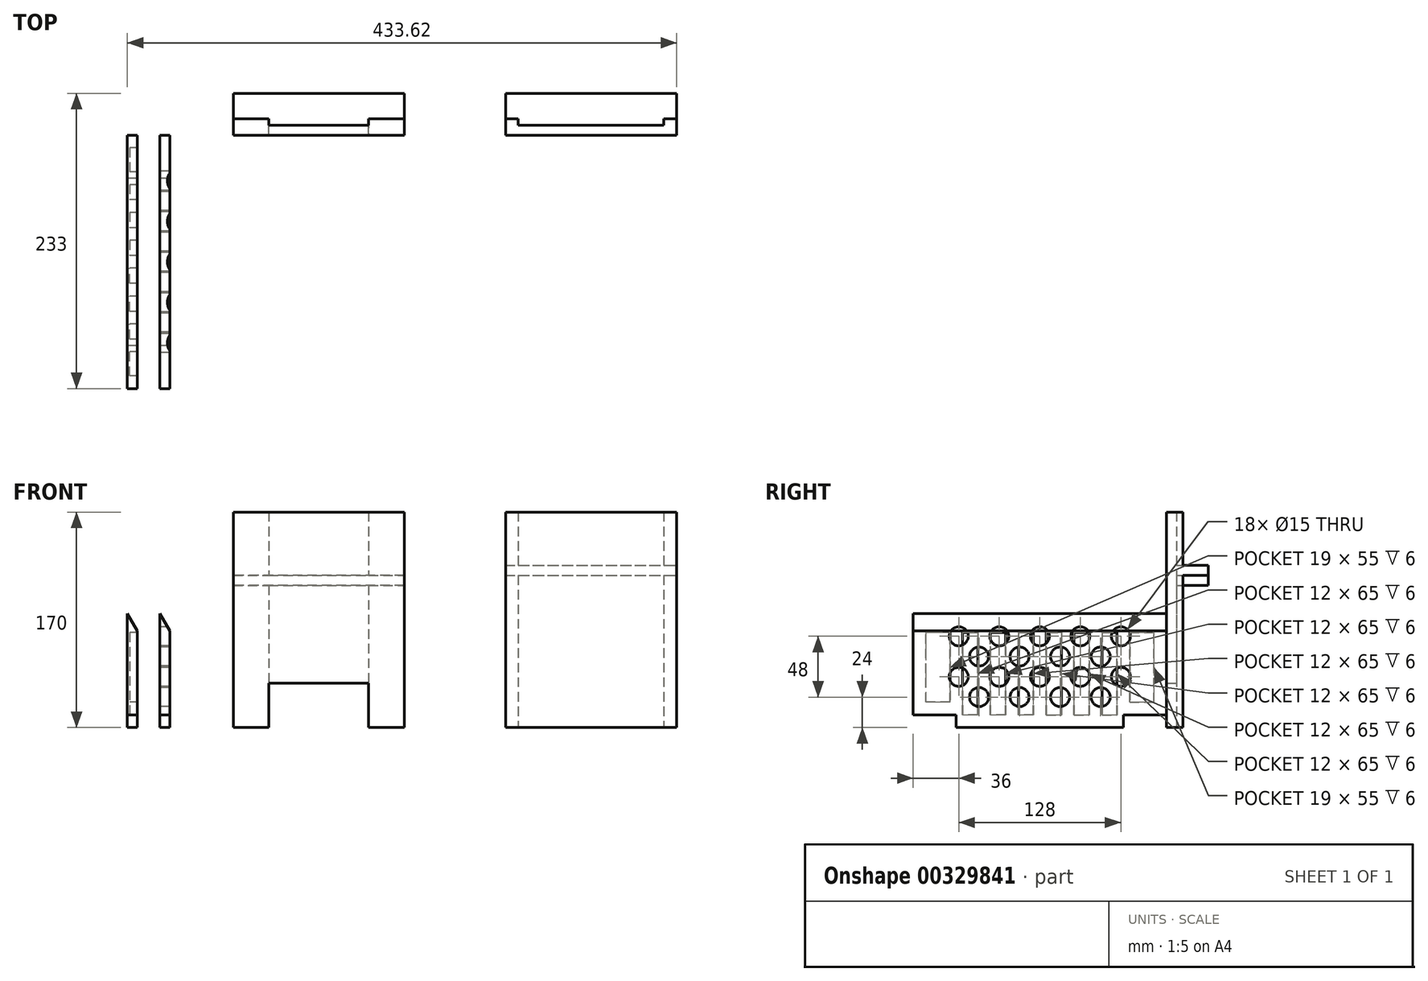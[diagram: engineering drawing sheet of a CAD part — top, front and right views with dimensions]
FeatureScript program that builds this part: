
annotation { "Feature Type Name" : "Feature", "Feature Type Description" : "" }
export const myFeature = defineFeature(function(context is Context, id is Id, definition is map)
    precondition{}
    {
        {
            var Q0;
            Q0=qCreatedBy(makeId("Top.planeOp"),FACE);
            var sketch = newSketch(context, id + "F0", { "sketchPlane" : qUnion([Q0])});
            skLineSegment(sketch, "E0", {"start": v(40, 13) * mm, "end": v(40, 0) * mm});
            skLineSegment(sketch, "E1", {"start": v(40, 0) * mm, "end": v(175, 0) * mm});
            skLineSegment(sketch, "E2", {"start": v(175, 0) * mm, "end": v(175, 13) * mm});
            skLineSegment(sketch, "E3", {"start": v(175, 13) * mm, "end": v(165, 13) * mm});
            skLineSegment(sketch, "E4", {"start": v(165, 13) * mm, "end": v(165, 8) * mm});
            skLineSegment(sketch, "E5", {"start": v(165, 8) * mm, "end": v(50, 8) * mm});
            skLineSegment(sketch, "E6", {"start": v(50, 8) * mm, "end": v(50, 13) * mm});
            skLineSegment(sketch, "E7", {"start": v(50, 13) * mm, "end": v(40, 13) * mm});
            skSolve(sketch);
        }
        {
            var Q0;
            Q0 = qSketchRegion(id + "F0", true);
            extrude(context, id + "F1", {"entities" : qUnion([Q0]), "depth" : 170 * mm, "offsetDistance" : 25 * mm});
        }
        {
            var Q0;
            Q0=makeQuery(id+"F1.opExtrude","CAP_FACE",FACE,{"disambiguationData":[OSD([sQuery(id+"F0.wireOp",EDGE,"E0"),sQuery(id+"F0.wireOp",EDGE,"E1"),sQuery(id+"F0.wireOp",EDGE,"E2"),sQuery(id+"F0.wireOp",EDGE,"E3"),sQuery(id+"F0.wireOp",EDGE,"E4"),sQuery(id+"F0.wireOp",EDGE,"E5"),sQuery(id+"F0.wireOp",EDGE,"E6"),sQuery(id+"F0.wireOp",EDGE,"E7")])],"isStart":true});
            cPlane(context, id + "F2", {"entities" : qUnion([Q0]), "cplaneType" : CPlaneType.OFFSET, "offset" : 120 * mm, "oppositeDirection" : true, "width" : 150 * mm, "height" : 150 * mm});
        }
        {
            var Q0;
            Q0=qCreatedBy(id+"F2.planeOp",FACE);
            var sketch = newSketch(context, id + "F3", { "sketchPlane" : qUnion([Q0])});
            skLineSegment(sketch, "E8.bottom", {"start": v(40, 0) * mm, "end": v(175, 0) * mm});
            skLineSegment(sketch, "E8.top", {"start": v(40, -33) * mm, "end": v(175, -33) * mm});
            skLineSegment(sketch, "E8.left", {"start": v(40, 0) * mm, "end": v(40, -33) * mm});
            skLineSegment(sketch, "E8.right", {"start": v(175, 0) * mm, "end": v(175, -33) * mm});
            skSolve(sketch);
        }
        {
            var Q0;
            Q0 = qSketchRegion(id + "F3", true);
            extrude(context, id + "F4", {"entities" : qUnion([Q0]), "operationType" : NewBodyOperationType.ADD, "oppositeDirection" : true, "depth" : 8 * mm, "offsetDistance" : 25 * mm});
        }
        {
            var Q0;
            Q0=qCreatedBy(makeId("Top.planeOp"),FACE);
            var sketch = newSketch(context, id + "F5", { "sketchPlane" : qUnion([Q0])});
            skLineSegment(sketch, "E9", {"start": v(-40, 0) * mm, "end": v(-40, 13) * mm});
            skLineSegment(sketch, "E10", {"start": v(-40, 13) * mm, "end": v(-68, 13) * mm});
            skLineSegment(sketch, "E11", {"start": v(-68, 13) * mm, "end": v(-68, 8) * mm});
            skLineSegment(sketch, "E12", {"start": v(-68, 8) * mm, "end": v(-147, 8) * mm});
            skLineSegment(sketch, "E13", {"start": v(-147, 8) * mm, "end": v(-147, 13) * mm});
            skLineSegment(sketch, "E14", {"start": v(-147, 13) * mm, "end": v(-175, 13) * mm});
            skLineSegment(sketch, "E15", {"start": v(-175, 13) * mm, "end": v(-175, 0) * mm});
            skLineSegment(sketch, "E16", {"start": v(-175, 0) * mm, "end": v(-40, 0) * mm});
            skSolve(sketch);
        }
        {
            var Q0;
            Q0 = qSketchRegion(id + "F5", true);
            extrude(context, id + "F6", {"entities" : qUnion([Q0]), "depth" : 170 * mm, "offsetDistance" : 25 * mm});
        }
        {
            var Q0;
            Q0=makeQuery(id+"F6.opExtrude","SWEPT_FACE",FACE,{"disambiguationData":[OSD([sQuery(id+"F5.wireOp",EDGE,"E12")])]});
            var sketch = newSketch(context, id + "F7", { "sketchPlane" : qUnion([Q0])});
            skLineSegment(sketch, "E17.bottom", {"start": v(68, 0) * mm, "end": v(147, 0) * mm});
            skLineSegment(sketch, "E17.top", {"start": v(68, 35) * mm, "end": v(147, 35) * mm});
            skLineSegment(sketch, "E17.left", {"start": v(68, 0) * mm, "end": v(68, 35) * mm});
            skLineSegment(sketch, "E17.right", {"start": v(147, 0) * mm, "end": v(147, 35) * mm});
            skSolve(sketch);
        }
        {
            var Q0;
            Q0 = qSketchRegion(id + "F7", true);
            extrude(context, id + "F8", {"entities" : qUnion([Q0]), "operationType" : NewBodyOperationType.REMOVE, "endBound" : BoundingType.UP_TO_NEXT, "oppositeDirection" : true, "depth" : 25 * mm, "offsetDistance" : 25 * mm});
        }
        {
            var Q0;
            Q0=qCreatedBy(id+"F2.planeOp",FACE);
            var sketch = newSketch(context, id + "F9", { "sketchPlane" : qUnion([Q0])});
            skLineSegment(sketch, "E18.bottom", {"start": v(-40, 0) * mm, "end": v(-175, 0) * mm});
            skLineSegment(sketch, "E18.top", {"start": v(-40, -33) * mm, "end": v(-175, -33) * mm});
            skLineSegment(sketch, "E18.left", {"start": v(-40, 0) * mm, "end": v(-40, -33) * mm});
            skLineSegment(sketch, "E18.right", {"start": v(-175, 0) * mm, "end": v(-175, -33) * mm});
            skSolve(sketch);
        }
        {
            var Q0;
            Q0 = qSketchRegion(id + "F9", true);
            extrude(context, id + "F10", {"entities" : qUnion([Q0]), "operationType" : NewBodyOperationType.ADD, "depth" : 8 * mm, "offsetDistance" : 25 * mm});
        }
        {
            var Q0;
            Q0=qCreatedBy(makeId("Front.planeOp"),FACE);
            var sketch = newSketch(context, id + "F11", { "sketchPlane" : qUnion([Q0])});
            skLineSegment(sketch, "E19.bottom", {"start": v(-225, 0) * mm, "end": v(-233, 0) * mm});
            skLineSegment(sketch, "E19.left", {"start": v(-225, 0) * mm, "end": v(-225, 76.14) * mm});
            skLineSegment(sketch, "E19.right", {"start": v(-233, 0) * mm, "end": v(-233, 90) * mm});
            skLineSegment(sketch, "E20", {"start": v(-233, 90) * mm, "end": v(-225, 76.14) * mm});
            skSolve(sketch);
        }
        {
            var Q0;
            Q0 = qSketchRegion(id + "F11", true);
            extrude(context, id + "F12", {"entities" : qUnion([Q0]), "depth" : 200 * mm, "offsetDistance" : 25 * mm});
        }
        {
            var Q0;
            Q0=makeQuery(id+"F12.opExtrude","SWEPT_FACE",FACE,{"disambiguationData":[OSD([sQuery(id+"F11.wireOp",EDGE,"E19.right")])]});
            var sketch = newSketch(context, id + "F13", { "sketchPlane" : qUnion([Q0])});
            skLineSegment(sketch, "E21.bottom", {"start": v(0, 0) * mm, "end": v(34, 0) * mm});
            skLineSegment(sketch, "E21.top", {"start": v(0, 10) * mm, "end": v(34, 10) * mm});
            skLineSegment(sketch, "E21.left", {"start": v(0, 0) * mm, "end": v(0, 10) * mm});
            skLineSegment(sketch, "E21.right", {"start": v(34, 0) * mm, "end": v(34, 10) * mm});
            skLineSegment(sketch, "E22.bottom", {"start": v(200, 0) * mm, "end": v(166, 0) * mm});
            skLineSegment(sketch, "E22.top", {"start": v(200, 10) * mm, "end": v(166, 10) * mm});
            skLineSegment(sketch, "E22.left", {"start": v(200, 0) * mm, "end": v(200, 10) * mm});
            skLineSegment(sketch, "E22.right", {"start": v(166, 0) * mm, "end": v(166, 10) * mm});
            skCircle(sketch, "E23", {"center": v(36, 72) * mm, "radius": 7.5 * mm});
            skCircle(sketch, "E24", {"center": v(52, 56) * mm, "radius": 7.5 * mm});
            skCircle(sketch, "E25.0.1.0", {"center": v(36, 40) * mm, "radius": 7.5 * mm});
            skCircle(sketch, "E25.0.1.1", {"center": v(52, 24) * mm, "radius": 7.5 * mm});
            skCircle(sketch, "E25.1.0.0", {"center": v(68, 72) * mm, "radius": 7.5 * mm});
            skCircle(sketch, "E25.1.0.1", {"center": v(84, 56) * mm, "radius": 7.5 * mm});
            skCircle(sketch, "E25.1.1.0", {"center": v(68, 40) * mm, "radius": 7.5 * mm});
            skCircle(sketch, "E25.1.1.1", {"center": v(84, 24) * mm, "radius": 7.5 * mm});
            skCircle(sketch, "E25.2.0.0", {"center": v(100, 72) * mm, "radius": 7.5 * mm});
            skCircle(sketch, "E25.2.0.1", {"center": v(116, 56) * mm, "radius": 7.5 * mm});
            skCircle(sketch, "E25.2.1.0", {"center": v(100, 40) * mm, "radius": 7.5 * mm});
            skCircle(sketch, "E25.2.1.1", {"center": v(116, 24) * mm, "radius": 7.5 * mm});
            skCircle(sketch, "E25.3.0.0", {"center": v(132, 72) * mm, "radius": 7.5 * mm});
            skCircle(sketch, "E25.3.0.1", {"center": v(148, 56) * mm, "radius": 7.5 * mm});
            skCircle(sketch, "E25.3.1.0", {"center": v(132, 40) * mm, "radius": 7.5 * mm});
            skCircle(sketch, "E25.3.1.1", {"center": v(148, 24) * mm, "radius": 7.5 * mm});
            skCircle(sketch, "E25.4.0.0", {"center": v(164, 72) * mm, "radius": 7.5 * mm});
            skCircle(sketch, "E25.4.1.0", {"center": v(164, 40) * mm, "radius": 7.5 * mm});
            skLineSegment(sketch, "E25.direction1", {"start": v(36, 72) * mm, "end": v(68, 72) * mm, "construction": true});
            skLineSegment(sketch, "E25.direction2", {"start": v(36, 72) * mm, "end": v(36, 40) * mm, "construction": true});
            skLineSegment(sketch, "E26", {"start": v(52, 72) * mm, "end": v(52, 56) * mm, "construction": true});
            skLineSegment(sketch, "E27", {"start": v(36, 56) * mm, "end": v(52, 56) * mm, "construction": true});
            skSolve(sketch);
        }
        {
            var Q0;
            Q0 = qSketchRegion(id + "F13", true);
            extrude(context, id + "F14", {"entities" : qUnion([Q0]), "operationType" : NewBodyOperationType.REMOVE, "endBound" : BoundingType.UP_TO_NEXT, "oppositeDirection" : true, "depth" : 25 * mm, "offsetDistance" : 25 * mm});
        }
        {
            var Q0;
            Q0=qCreatedBy(makeId("Front.planeOp"),FACE);
            var sketch = newSketch(context, id + "F15", { "sketchPlane" : qUnion([Q0])});
            skLineSegment(sketch, "E28", {"start": v(-250.62, 0) * mm, "end": v(-250.62, 76.14) * mm});
            skLineSegment(sketch, "E29", {"start": v(-250.62, 76.14) * mm, "end": v(-258.62, 90) * mm});
            skLineSegment(sketch, "E30", {"start": v(-258.62, 90) * mm, "end": v(-258.62, 0) * mm});
            skLineSegment(sketch, "E31", {"start": v(-258.62, 0) * mm, "end": v(-250.62, 0) * mm});
            skSolve(sketch);
        }
        {
            var Q0;
            Q0 = qSketchRegion(id + "F15", true);
            extrude(context, id + "F16", {"entities" : qUnion([Q0]), "depth" : 200 * mm, "offsetDistance" : 25 * mm});
        }
        {
            var Q0;
            Q0=makeQuery(id+"F16.opExtrude","SWEPT_FACE",FACE,{"disambiguationData":[OSD([sQuery(id+"F15.wireOp",EDGE,"E30")])]});
            var sketch = newSketch(context, id + "F17", { "sketchPlane" : qUnion([Q0])});
            skLineSegment(sketch, "E32.bottom", {"start": v(0, 0) * mm, "end": v(34, 0) * mm});
            skLineSegment(sketch, "E32.top", {"start": v(0, 10) * mm, "end": v(34, 10) * mm});
            skLineSegment(sketch, "E32.left", {"start": v(0, 0) * mm, "end": v(0, 10) * mm});
            skLineSegment(sketch, "E32.right", {"start": v(34, 0) * mm, "end": v(34, 10) * mm});
            skLineSegment(sketch, "E33.bottom", {"start": v(200, 0) * mm, "end": v(166, 0) * mm});
            skLineSegment(sketch, "E33.top", {"start": v(200, 10) * mm, "end": v(166, 10) * mm});
            skLineSegment(sketch, "E33.left", {"start": v(200, 0) * mm, "end": v(200, 10) * mm});
            skLineSegment(sketch, "E33.right", {"start": v(166, 0) * mm, "end": v(166, 10) * mm});
            skPoint(sketch, "E34.1", {"position": v(166, 10) * mm});
            skPoint(sketch, "E35.0", {"position": v(34, 10) * mm});
            skSolve(sketch);
        }
        {
            var Q0;
            Q0 = qSketchRegion(id + "F17", true);
            extrude(context, id + "F18", {"entities" : qUnion([Q0]), "operationType" : NewBodyOperationType.REMOVE, "endBound" : BoundingType.UP_TO_NEXT, "oppositeDirection" : true, "depth" : 25 * mm, "offsetDistance" : 25 * mm});
        }
        {
            var Q0;
            Q0=makeQuery(id+"F16.opExtrude","SWEPT_FACE",FACE,{"disambiguationData":[OSD([sQuery(id+"F15.wireOp",EDGE,"E30")])]});
            cPlane(context, id + "F19", {"entities" : qUnion([Q0]), "cplaneType" : CPlaneType.OFFSET, "offset" : 2 * mm, "oppositeDirection" : true, "width" : 150 * mm, "height" : 150 * mm});
        }
        {
            var Q0;
            Q0=qCreatedBy(id+"F19.planeOp",FACE);
            var sketch = newSketch(context, id + "F20", { "sketchPlane" : qUnion([Q0])});
            skLineSegment(sketch, "E36.bottom", {"start": v(10, 75) * mm, "end": v(29, 75) * mm});
            skLineSegment(sketch, "E36.top", {"start": v(10, 20) * mm, "end": v(29, 20) * mm});
            skLineSegment(sketch, "E36.left", {"start": v(10, 75) * mm, "end": v(10, 20) * mm});
            skLineSegment(sketch, "E36.right", {"start": v(29, 75) * mm, "end": v(29, 20) * mm});
            skLineSegment(sketch, "E37.bottom", {"start": v(39, 75) * mm, "end": v(51, 75) * mm});
            skLineSegment(sketch, "E37.top", {"start": v(39, 10) * mm, "end": v(51, 10) * mm});
            skLineSegment(sketch, "E37.left", {"start": v(39, 75) * mm, "end": v(39, 10) * mm});
            skLineSegment(sketch, "E37.right", {"start": v(51, 75) * mm, "end": v(51, 10) * mm});
            skLineSegment(sketch, "E38.1.0.0", {"start": v(61, 75) * mm, "end": v(73, 75) * mm});
            skLineSegment(sketch, "E38.1.0.1", {"start": v(61, 75) * mm, "end": v(61, 10) * mm});
            skLineSegment(sketch, "E38.1.0.2", {"start": v(73, 75) * mm, "end": v(73, 10) * mm});
            skLineSegment(sketch, "E38.1.0.3", {"start": v(61, 10) * mm, "end": v(73, 10) * mm});
            skLineSegment(sketch, "E38.2.0.0", {"start": v(83, 75) * mm, "end": v(95, 75) * mm});
            skLineSegment(sketch, "E38.2.0.1", {"start": v(83, 75) * mm, "end": v(83, 10) * mm});
            skLineSegment(sketch, "E38.2.0.2", {"start": v(95, 75) * mm, "end": v(95, 10) * mm});
            skLineSegment(sketch, "E38.2.0.3", {"start": v(83, 10) * mm, "end": v(95, 10) * mm});
            skLineSegment(sketch, "E39", {"start": v(100, 90) * mm, "end": v(100, 0) * mm, "construction": true});
            skLineSegment(sketch, "E40.MirrorCS", {"start": v(117, 75) * mm, "end": v(105, 75) * mm});
            skLineSegment(sketch, "E41.MirrorCS", {"start": v(117, 75) * mm, "end": v(117, 10) * mm});
            skLineSegment(sketch, "E42.MirrorCS", {"start": v(105, 75) * mm, "end": v(105, 10) * mm});
            skLineSegment(sketch, "E43.MirrorCS", {"start": v(117, 10) * mm, "end": v(105, 10) * mm});
            skLineSegment(sketch, "E44.MirrorCS", {"start": v(127, 75) * mm, "end": v(127, 10) * mm});
            skLineSegment(sketch, "E45.MirrorCS", {"start": v(139, 10) * mm, "end": v(127, 10) * mm});
            skLineSegment(sketch, "E46.MirrorCS", {"start": v(139, 75) * mm, "end": v(139, 10) * mm});
            skLineSegment(sketch, "E47.MirrorCS", {"start": v(139, 75) * mm, "end": v(127, 75) * mm});
            skLineSegment(sketch, "E48.MirrorCS", {"start": v(161, 75) * mm, "end": v(161, 10) * mm});
            skLineSegment(sketch, "E49.MirrorCS", {"start": v(149, 75) * mm, "end": v(149, 10) * mm});
            skLineSegment(sketch, "E50.MirrorCS", {"start": v(161, 10) * mm, "end": v(149, 10) * mm});
            skLineSegment(sketch, "E51.MirrorCS", {"start": v(190, 75) * mm, "end": v(171, 75) * mm});
            skLineSegment(sketch, "E52.MirrorCS", {"start": v(190, 75) * mm, "end": v(190, 20) * mm});
            skLineSegment(sketch, "E53.MirrorCS", {"start": v(171, 75) * mm, "end": v(171, 20) * mm});
            skLineSegment(sketch, "E54.MirrorCS", {"start": v(190, 20) * mm, "end": v(171, 20) * mm});
            skLineSegment(sketch, "E55", {"start": v(149, 75) * mm, "end": v(161, 75) * mm});
            skLineSegment(sketch, "E56", {"start": v(51, 75) * mm, "end": v(61, 75) * mm, "construction": true});
            skLineSegment(sketch, "E57", {"start": v(95, 75) * mm, "end": v(105, 75) * mm, "construction": true});
            skLineSegment(sketch, "E58", {"start": v(73, 75) * mm, "end": v(83, 75) * mm, "construction": true});
            skSolve(sketch);
        }
        {
            var Q0;
            Q0 = qSketchRegion(id + "F20", true);
            var Q1;
            Q1=makeQuery(id+"F16.opExtrude","SWEPT_FACE",FACE,{"disambiguationData":[OSD([sQuery(id+"F15.wireOp",EDGE,"E28")])]});
            extrude(context, id + "F21", {"entities" : qUnion([Q0]), "operationType" : NewBodyOperationType.REMOVE, "endBound" : BoundingType.UP_TO_SURFACE, "oppositeDirection" : true, "depth" : 7 * mm, "endBoundEntityFace" : qUnion([Q1]), "offsetDistance" : 25 * mm});
        }
    });
